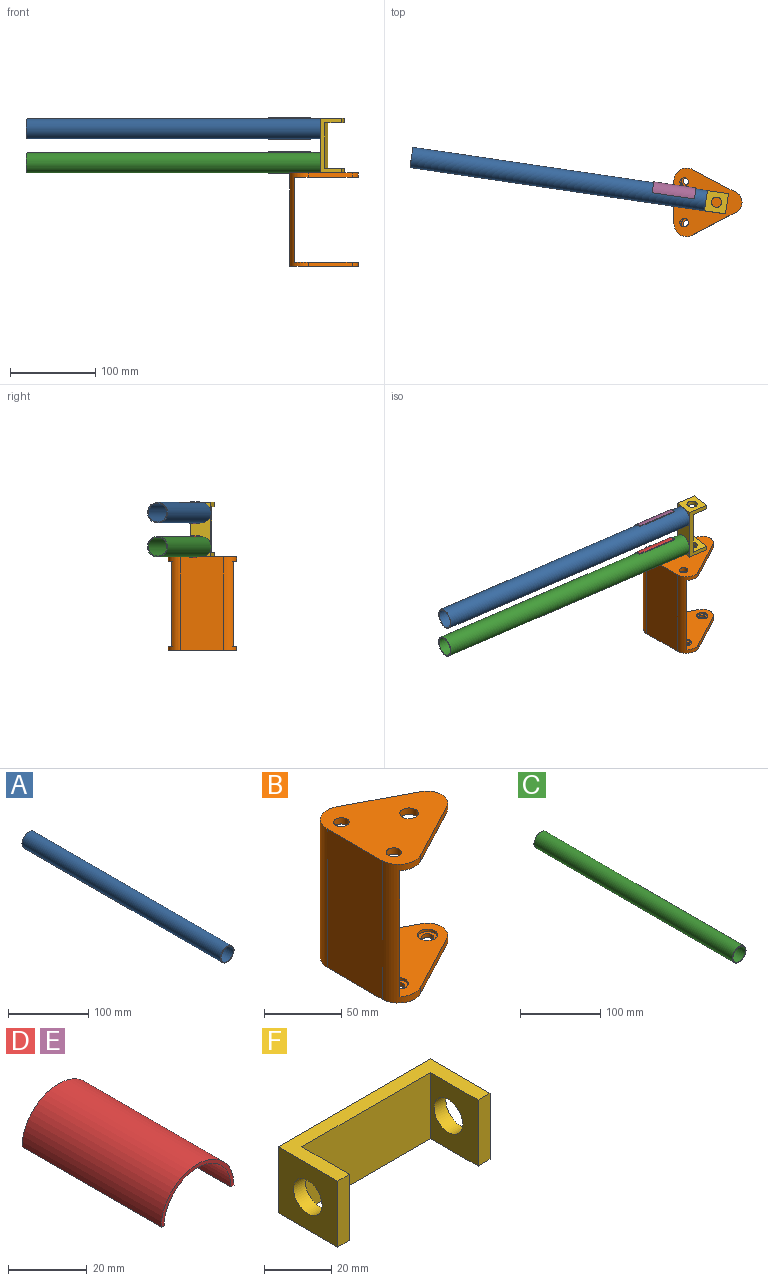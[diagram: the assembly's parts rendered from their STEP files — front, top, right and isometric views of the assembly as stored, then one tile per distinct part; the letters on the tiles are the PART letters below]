
ASSEMBLY  parts=6 mates=6
PART A: 4 faces, bbox 24x350x24 mm
  f0: cylinder r=12mm len=350mm, axis (0,-1,0), area 26389.4mm2, adj f2,f3
  f1: cylinder r=11mm len=350mm, axis (0,-1,0), area 24190.3mm2, adj f2,f3
  f2: plane 24x24mm, normal (0,1,0), area 72.3mm2, adj f0,f1
  f3: plane 24x24mm, normal (0,-1,0), area 72.3mm2, adj f0,f1
PART B: 26 faces, bbox 80x80.3x110 mm
  f0: cylinder r=4mm len=8mm, axis (0,0,-1), area 75.4mm2, adj f8,f25
  f1: cylinder r=4mm len=8mm, axis (0,0,-1), area 75.4mm2, adj f8,f23
  f2: cylinder r=4mm len=8mm, axis (0,0,-1), area 75.4mm2, adj f8,f21
  f3: plane 51.06x26.88mm, normal (0.47,-0.88,0), area 288.5mm2, adj f5,f6,f14,f19
  f4: plane 51.06x26.88mm, normal (0.47,0.88,0), area 288.5mm2, adj f8,f9,f15,f18
  f5: plane 80.34x80mm, normal (0,0,1), area 4058.7mm2, adj f3,f7,f11,f12,f14,f16,f17,f18
  f6: plane 80.34x75mm, normal (0,0,-1), area 3729.4mm2, adj f3,f10,f11,f12,f14,f16,f17,f18
  f7: plane 110x50.39mm, normal (-1,0,0), area 5542.7mm2, adj f5,f8,f18,f19
  f8: plane 80.34x80mm, normal (0,0,-1), area 4178mm2, adj f0,f1,f2,f4,f7,f13,f15,f18
  f9: plane 80.34x75mm, normal (0,0,1), area 3601.3mm2, adj f4,f10,f13,f15,f18,f19,f20,f22
  f10: plane 100x72.73mm, normal (1,0,0), area 7272.8mm2, adj f6,f9,f18,f19
  f11: cylinder r=6mm len=12mm, axis (0,0,1), area 188.5mm2, adj f5,f6
  f12: plane 51.06x26.88mm, normal (0.47,0.88,0), area 288.5mm2, adj f5,f6,f14,f18
  f13: plane 51.06x26.88mm, normal (0.47,-0.88,0), area 288.5mm2, adj f8,f9,f15,f19
  f14: cylinder r=13.08mm len=23.14mm, axis (0,0,1), area 142.1mm2, adj f3,f5,f6,f12
  f15: cylinder r=13.08mm len=23.14mm, axis (0,0,1), area 142.1mm2, adj f4,f8,f9,f13
  f16: cylinder r=5mm len=10mm, axis (0,0,1), area 157.1mm2, adj f5,f6
  f17: cylinder r=5mm len=10mm, axis (0,0,1), area 157.1mm2, adj f5,f6
  f18: cylinder r=14.98mm len=110mm, axis (0,0,-1), area 1568.5mm2, adj f4,f5,f6,f7,f8,f9,f10,f12
  f19: cylinder r=14.98mm len=110mm, axis (0,0,-1), area 1568.5mm2, adj f3,f5,f6,f7,f8,f9,f10,f13
  f20: cylinder r=6.5mm len=13mm, axis (0,0,1), area 81.7mm2, adj f9,f21
  f21: plane 13x13mm, normal (0,0,1), area 82.5mm2, adj f2,f20
  f22: cylinder r=6.5mm len=13mm, axis (0,0,1), area 81.7mm2, adj f9,f23
  f23: plane 13x13mm, normal (0,0,1), area 82.5mm2, adj f1,f22
  f24: cylinder r=6.5mm len=13mm, axis (0,0,1), area 81.7mm2, adj f9,f25
  f25: plane 13x13mm, normal (0,0,1), area 82.5mm2, adj f0,f24
PART C: 4 faces, bbox 24x350x24 mm
  f0: cylinder r=11mm len=350mm, axis (0,-1,0), area 24190.3mm2, adj f2,f3
  f1: cylinder r=12mm len=350mm, axis (0,-1,0), area 26389.4mm2, adj f2,f3
  f2: plane 24x24mm, normal (0,1,0), area 72.3mm2, adj f0,f1
  f3: plane 24x24mm, normal (0,-1,0), area 72.3mm2, adj f0,f1
PART D: 6 faces, bbox 26.2x50x13.1 mm
  f0: plane 50x1.09mm, normal (0,0,-1), area 54.5mm2, adj f1,f3,f4,f5
  f1: cylinder r=12mm len=50mm, axis (0,1,0), area 1885mm2, adj f0,f2,f4,f5
  f2: plane 50x1.09mm, normal (0,0,-1), area 54.5mm2, adj f1,f3,f4,f5
  f3: cylinder r=13.09mm len=50mm, axis (0,1,0), area 2056.3mm2, adj f0,f2,f4,f5
  f4: plane 26.18x13.09mm, normal (0,-1,0), area 43mm2, adj f0,f1,f2,f3
  f5: plane 26.18x13.09mm, normal (0,1,0), area 43mm2, adj f0,f1,f2,f3
PART E: same geometry as D
PART F: 12 faces, bbox 64x25x24 mm
  f0: plane 64x25mm, normal (0,0,-1), area 520mm2, adj f1,f3,f5,f6,f7,f9,f10,f11
  f1: plane 24x5mm, normal (0,-1,0), area 120mm2, adj f0,f4,f5,f9
  f2: cylinder r=6mm len=12mm, axis (1,0,0), area 188.5mm2, adj f5,f9
  f3: plane 25x24mm, normal (1,0,0), area 486.9mm2, adj f0,f4,f6,f7,f8
  f4: plane 64x25mm, normal (0,0,1), area 520mm2, adj f1,f3,f5,f6,f7,f9,f10,f11
  f5: plane 25x24mm, normal (-1,0,0), area 486.9mm2, adj f0,f1,f2,f4,f7
  f6: plane 24x5mm, normal (0,-1,0), area 120mm2, adj f0,f3,f4,f10
  f7: plane 64x24mm, normal (0,1,0), area 1536mm2, adj f0,f3,f4,f5
  f8: cylinder r=6mm len=12mm, axis (1,0,0), area 188.5mm2, adj f3,f10
  f9: plane 24x20mm, normal (1,0,0), area 366.9mm2, adj f0,f1,f2,f4,f11
  f10: plane 24x20mm, normal (-1,0,0), area 366.9mm2, adj f0,f4,f6,f8,f11
  f11: plane 54x24mm, normal (0,-1,0), area 1296mm2, adj f0,f4,f9,f10
PLACE A rot(axis=(0.65,-0.76,0),180deg) t=(-8.03,28.44,118.18)mm
PLACE B t=(1.43,6.84,6.18)mm fixed
PLACE C rot(axis=(0.65,-0.76,0),180deg) t=(-13.84,-11.14,78.18)mm
PLACE D rot(axis=(-0.6,-0.52,-0.6),124.9deg) t=(-49.37,14.3,78.18)mm
PLACE E rot(axis=(-0.6,-0.52,-0.6),124.9deg) t=(-49.37,14.3,118.18)mm
PLACE F rot(axis=(-0.55,0.63,0.55),115.3deg) t=(-10.93,8.65,98.18)mm
MATE slider D.f1 <-> C.f0  axis (-0.99,0.15,0) through (-74.11,17.93,78.18)mm
MATE slider E.f1 <-> A.f0  axis (-0.99,0.15,0) through (-74.11,17.93,118.18)mm
MATE fastened A.f0 <-> F.f7  axis (0.99,-0.15,0) through (-10.93,8.65,118.18)mm
MATE fastened C.f0 <-> F.f7  axis (0.99,-0.15,0) through (-10.93,8.65,78.18)mm
MATE fastened D.f4 <-> E.f4  axis (-0.99,0.15,0) through (-72.95,25.84,78.18)mm
MATE revolute F.f2 <-> B.f11  axis (0,0,-1) through (1.43,6.84,66.18)mm
